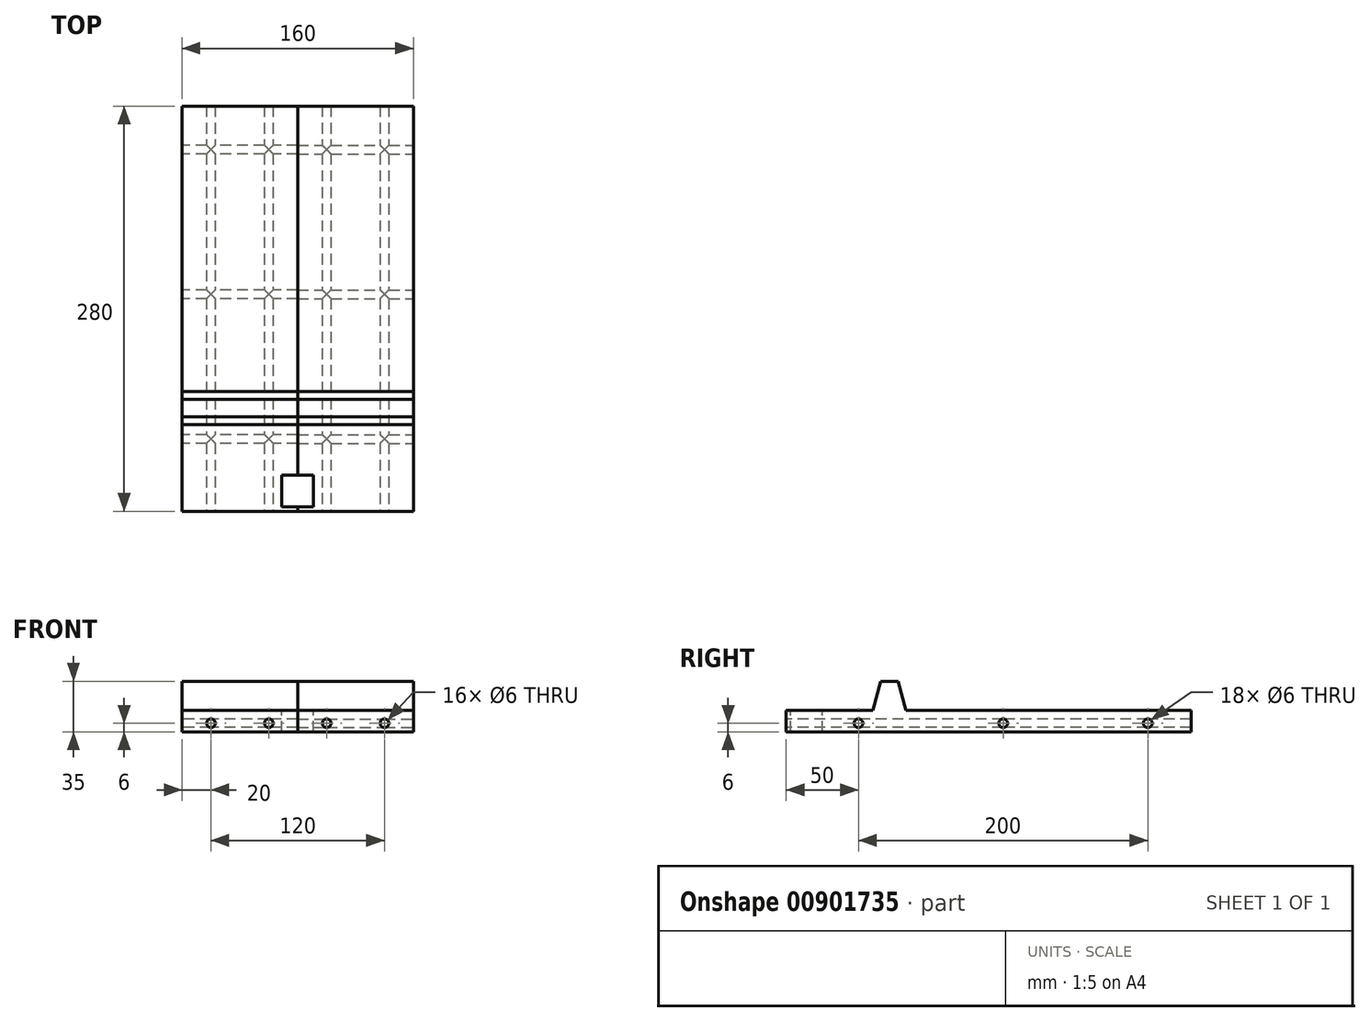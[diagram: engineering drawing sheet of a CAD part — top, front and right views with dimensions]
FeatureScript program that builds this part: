
annotation { "Feature Type Name" : "Feature", "Feature Type Description" : "" }
export const myFeature = defineFeature(function(context is Context, id is Id, definition is map)
    precondition{}
    {
        {
            var Q0;
            Q0=qCreatedBy(makeId("Top.planeOp"),FACE);
            var sketch = newSketch(context, id + "F0", { "sketchPlane" : qUnion([Q0])});
            skLineSegment(sketch, "E0.bottom", {"start": v(0, 0) * mm, "end": v(80, 0) * mm});
            skLineSegment(sketch, "E0.top", {"start": v(0, 280) * mm, "end": v(80, 280) * mm});
            skLineSegment(sketch, "E0.left", {"start": v(0, 0) * mm, "end": v(0, 280) * mm});
            skLineSegment(sketch, "E0.right", {"start": v(80, 0) * mm, "end": v(80, 280) * mm});
            skSolve(sketch);
        }
        {
            var Q0;
            Q0=makeQuery(id+"F0.imprint","IMPRINT",FACE,{"disambiguationData":[TD([[makeQuery(id+"F0.imprint","IMPRINT",EDGE,{"derivedFrom":sQuery(id+"F0.wireOp",EDGE,"E0.bottom")}),1.0]])]});
            extrude(context, id + "F1", {"entities" : qUnion([Q0]), "depth" : 15 * mm, "offsetDistance" : 25 * mm});
        }
        {
            var Q0;
            Q0=makeQuery(id+"F1.opExtrude","SWEPT_FACE",FACE,{"disambiguationData":[OSD([sQuery(id+"F0.wireOp",EDGE,"E0.right")])]});
            var sketch = newSketch(context, id + "F2", { "sketchPlane" : qUnion([Q0])});
            skLineSegment(sketch, "E1", {"start": v(60, 15) * mm, "end": v(65.36, 35) * mm});
            skLineSegment(sketch, "E2", {"start": v(65.36, 35) * mm, "end": v(77.36, 35) * mm});
            skLineSegment(sketch, "E3", {"start": v(77.36, 35) * mm, "end": v(82.72, 15) * mm});
            skLineSegment(sketch, "E4", {"start": v(60, 15) * mm, "end": v(82.72, 15) * mm});
            skSolve(sketch);
        }
        {
            var Q0;
            Q0=qSketchRegion(id+"F2",true);
            extrude(context, id + "F3", {"entities" : qUnion([Q0]), "operationType" : NewBodyOperationType.ADD, "oppositeDirection" : true, "depth" : 80 * mm, "offsetDistance" : 25 * mm});
        }
        {
            var Q0;
            {var subQ1=sQuery(id+"F0.wireOp",EDGE,"E0.left");var subQ2=sQuery(id+"F0.wireOp",EDGE,"E0.right");var subQ3=sQuery(id+"F0.wireOp",EDGE,"E0.bottom");Q0=makeQuery(id+"F3.boolean.opBoolean","SPLIT",FACE,{"disambiguationData":[TD([makeQuery(id+"F1.opExtrude","SWEPT_FACE",FACE,{"disambiguationData":[OSD([subQ3])]})])],"derivedFrom":makeQuery(id+"F1.opExtrude","CAP_FACE",FACE,{"disambiguationData":[OSD([subQ3,sQuery(id+"F0.wireOp",EDGE,"E0.top"),subQ1,subQ2])],"isStart":false})});}
            var sketch = newSketch(context, id + "F4", { "sketchPlane" : qUnion([Q0])});
            skLineSegment(sketch, "E5", {"start": v(11, 25) * mm, "end": v(0, 25) * mm});
            skLineSegment(sketch, "E6", {"start": v(11, 25) * mm, "end": v(11, 3) * mm});
            skLineSegment(sketch, "E7", {"start": v(11, 3) * mm, "end": v(0, 3) * mm});
            skLineSegment(sketch, "E8", {"start": v(0, 3) * mm, "end": v(0, 25) * mm});
            skSolve(sketch);
        }
        {
            var Q0;
            Q0=qSketchRegion(id+"F4",true);
            extrude(context, id + "F5", {"entities" : qUnion([Q0]), "operationType" : NewBodyOperationType.REMOVE, "endBound" : BoundingType.UP_TO_NEXT, "oppositeDirection" : true, "depth" : 25 * mm, "offsetDistance" : 25 * mm});
        }
        {
            var Q0;
            Q0=makeQuery(id+"F1.opExtrude","SWEPT_FACE",FACE,{"disambiguationData":[OSD([sQuery(id+"F0.wireOp",EDGE,"E0.bottom")])]});
            var sketch = newSketch(context, id + "F6", { "sketchPlane" : qUnion([Q0])});
            skSolve(sketch);
        }
        {
            var Q0;
            {var subQ0=sQuery(id+"F0.wireOp",EDGE,"E0.bottom");Q0=makeQuery(id+"F6.imprint","IMPRINT",FACE,{"disambiguationData":[TD([[makeQuery(id+"F6.imprint","IMPRINT",EDGE,{"derivedFrom":makeQuery(id+"F1.opExtrude","CAP_EDGE",EDGE,{"disambiguationData":[OSD([subQ0])],"isStart":true})}),1.0]])]});}
            var sketch = newSketch(context, id + "F7", { "sketchPlane" : qUnion([Q0])});
            skCircle(sketch, "E9", {"center": v(60, 6) * mm, "radius": 3 * mm});
            skCircle(sketch, "E10", {"center": v(-491.18, 5.33) * mm, "radius": 6.56 * mm});
            skCircle(sketch, "E11", {"center": v(20, 6) * mm, "radius": 3 * mm});
            skSolve(sketch);
        }
        {
            var Q0;
            Q0=qSketchRegion(id+"F7",true);
            extrude(context, id + "F8", {"entities" : qUnion([Q0]), "operationType" : NewBodyOperationType.REMOVE, "endBound" : BoundingType.THROUGH_ALL, "oppositeDirection" : true, "depth" : 25 * mm, "offsetDistance" : 25 * mm});
        }
        {
            var Q0;
            Q0=makeQuery(id+"F3.boolean.opBoolean","MERGE",FACE,{"derivedFrom":[makeQuery(id+"F1.opExtrude","SWEPT_FACE",FACE,{"disambiguationData":[OSD([sQuery(id+"F0.wireOp",EDGE,"E0.right")])]}),makeQuery(id+"F3.opExtrude","CAP_FACE",FACE,{"disambiguationData":[OSD([sQuery(id+"F2.wireOp",EDGE,"E1"),sQuery(id+"F2.wireOp",EDGE,"E2"),sQuery(id+"F2.wireOp",EDGE,"E3"),sQuery(id+"F2.wireOp",EDGE,"E4")])],"isStart":true})]});
            var sketch = newSketch(context, id + "F9", { "sketchPlane" : qUnion([Q0])});
            skCircle(sketch, "E12", {"center": v(50, 6) * mm, "radius": 3 * mm});
            skCircle(sketch, "E13", {"center": v(250, 6) * mm, "radius": 3 * mm});
            skCircle(sketch, "E14", {"center": v(150, 6) * mm, "radius": 3 * mm});
            skSolve(sketch);
        }
        {
            var Q0;
            Q0=makeQuery(id+"F9.imprint","IMPRINT",FACE,{"disambiguationData":[TD([[makeQuery(id+"F9.imprint","IMPRINT",EDGE,{"derivedFrom":sQuery(id+"F9.wireOp",EDGE,"E12")}),1.0]])]});
            var Q1;
            Q1=makeQuery(id+"F9.imprint","IMPRINT",FACE,{"disambiguationData":[TD([[makeQuery(id+"F9.imprint","IMPRINT",EDGE,{"derivedFrom":sQuery(id+"F9.wireOp",EDGE,"E14")}),1.0]])]});
            var Q2;
            Q2=makeQuery(id+"F9.imprint","IMPRINT",FACE,{"disambiguationData":[TD([[makeQuery(id+"F9.imprint","IMPRINT",EDGE,{"derivedFrom":sQuery(id+"F9.wireOp",EDGE,"E13")}),1.0]])]});
            extrude(context, id + "F10", {"entities" : qUnion([Q0, Q1, Q2]), "operationType" : NewBodyOperationType.REMOVE, "endBound" : BoundingType.THROUGH_ALL, "oppositeDirection" : true, "depth" : 25 * mm, "offsetDistance" : 25 * mm});
        }
        {
            var Q0;
            Q0=makeQuery(id+"F1.opExtrude","SWEPT_BODY",BODY,{"disambiguationData":[OSD([sQuery(id+"F0.wireOp",EDGE,"E0.bottom"),sQuery(id+"F0.wireOp",EDGE,"E0.top"),sQuery(id+"F0.wireOp",EDGE,"E0.left"),sQuery(id+"F0.wireOp",EDGE,"E0.right")])]});
            var Q1;
            {var subQ0=sQuery(id+"F2.wireOp",EDGE,"E1");var subQ2=sQuery(id+"F0.wireOp",EDGE,"E0.left");var subQ3=sQuery(id+"F0.wireOp",EDGE,"E0.top");var subQ5=sQuery(id+"F2.wireOp",EDGE,"E2");var subQ6=sQuery(id+"F2.wireOp",EDGE,"E3");Q1=makeQuery(id+"F5.boolean.opBoolean","SPLIT",FACE,{"disambiguationData":[TD([makeQuery(id+"F1.opExtrude","SWEPT_FACE",FACE,{"disambiguationData":[OSD([subQ3])]})])],"derivedFrom":makeQuery(id+"F3.boolean.opBoolean","MERGE",FACE,{"derivedFrom":[makeQuery(id+"F1.opExtrude","SWEPT_FACE",FACE,{"disambiguationData":[OSD([subQ2])]}),makeQuery(id+"F3.opExtrude","CAP_FACE",FACE,{"disambiguationData":[OSD([subQ0,subQ5,subQ6,sQuery(id+"F2.wireOp",EDGE,"E4")])],"isStart":false})]})});}
            mirror(context, id + "F11", {"entities" : qUnion([Q0]), "mirrorPlane" : qUnion([Q1])});
        }
    });
